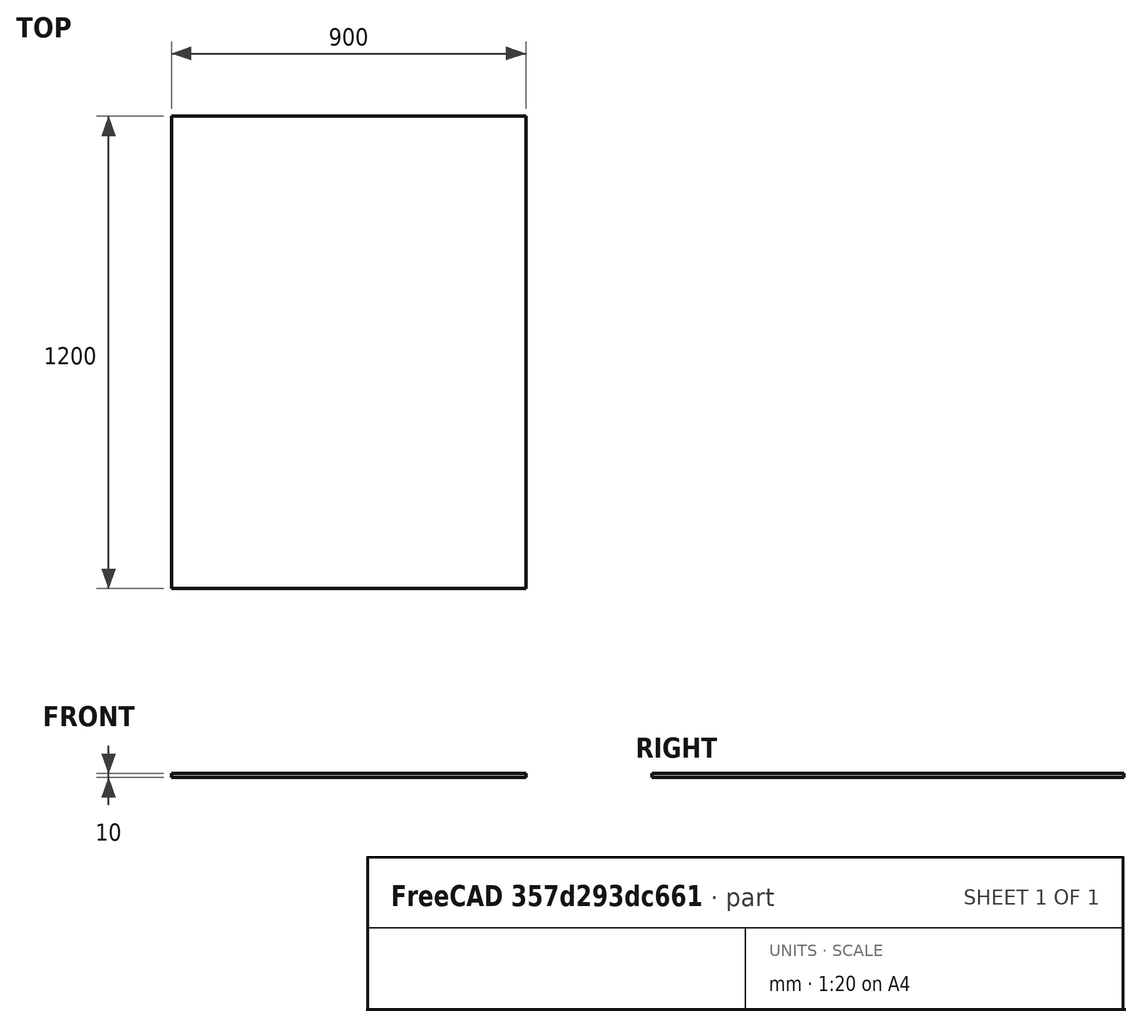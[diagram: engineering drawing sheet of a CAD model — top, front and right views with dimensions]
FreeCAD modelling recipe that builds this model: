
FCSTD DOCUMENT  (FreeCAD 0.20R29177 +426 (Git))
Label: plattform
License: All rights reserved
LicenseURL: http://en.wikipedia.org/wiki/All_rights_reserved
objects: Sketcher::SketchObject×1, PartDesign::Pad×1, PartDesign::Body×1
note: 4 computed .brp shape members not serialized (recipe doc carries the construction recipe); baked Part::Feature solids carry a one-line shape summary decoded from their .brp

FEATURE [Sketcher::SketchObject] Sketch
  FullyConstrained = true
  MapMode = 5
  Support = -> [XY_Plane]
  sketch-geometry (4):
    g0: LineSegment StartX=0 StartY=0 StartZ=0 EndX=900 EndY=0 EndZ=0
    g1: LineSegment StartX=900 StartY=0 StartZ=0 EndX=900 EndY=1200 EndZ=0
    g2: LineSegment StartX=900 StartY=1200 StartZ=0 EndX=0 EndY=1200 EndZ=0
    g3: LineSegment StartX=0 StartY=1200 StartZ=0 EndX=0 EndY=0 EndZ=0
  constraints (11):
    c: Coincident(g0,g1)
    c: Coincident(g1,g2)
    c: Coincident(g2,g3)
    c: Coincident(g3,g0)
    c: Horizontal(g0)
    c: Horizontal(g2)
    c: Vertical(g1)
    c: Vertical(g3)
    c: Coincident(g0,g-1)
    c: DistanceX(g2,g2) = 900  'fzg_breite'
    c: DistanceY(g3,g3) = 1200  'platte_laenge'
FEATURE [PartDesign::Pad] Pad
  Direction = (0,0,1)
  Length = 10
  Length2 = 10
  Profile = -> Sketch
  ReferenceAxis = -> Sketch [N_Axis]
  Refine = true
  Type = 0
FEATURE [PartDesign::Body] Body
  Group = -> [Sketch,Pad]
  Origin = -> Origin
  Tip = -> Pad
